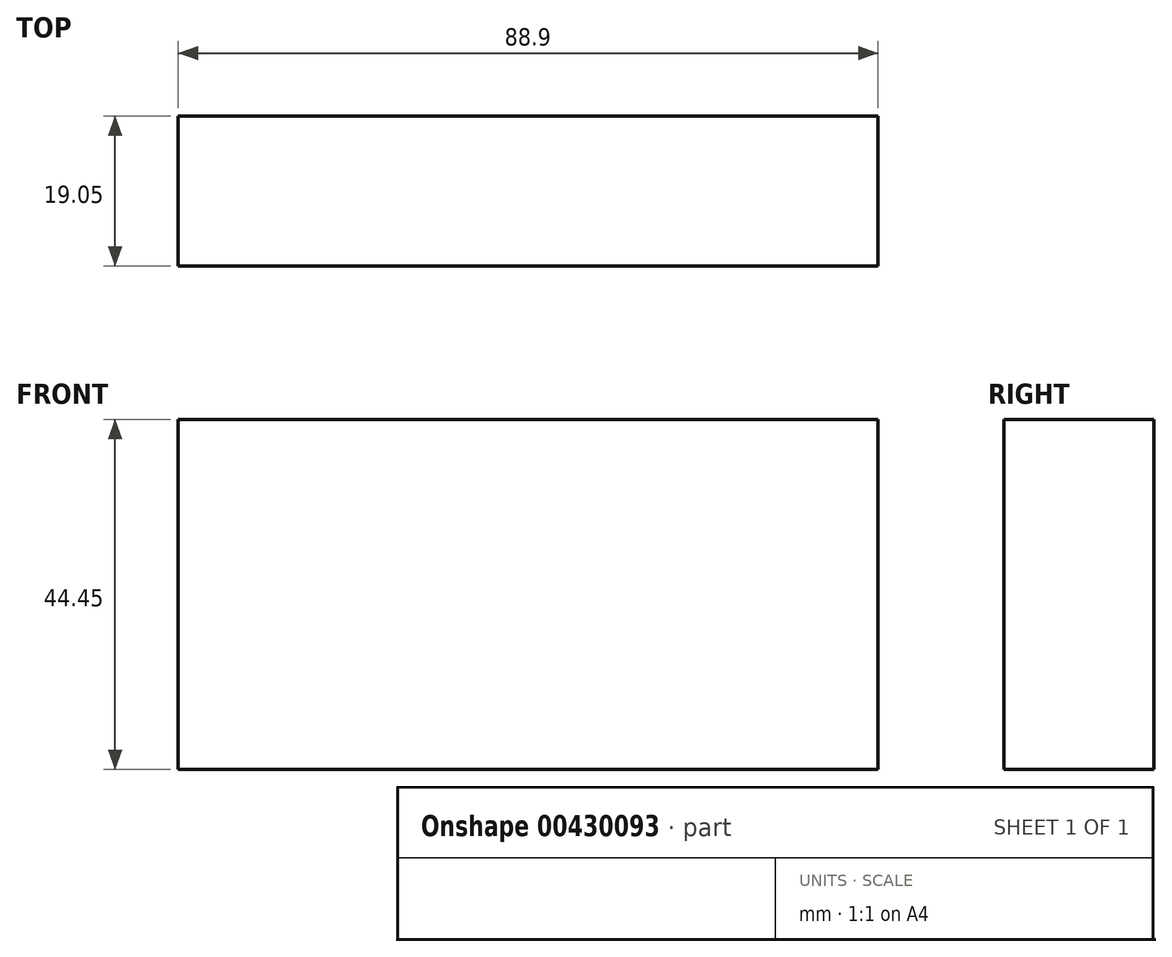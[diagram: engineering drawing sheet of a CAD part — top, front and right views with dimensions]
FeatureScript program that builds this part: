
annotation { "Feature Type Name" : "Feature", "Feature Type Description" : "" }
export const myFeature = defineFeature(function(context is Context, id is Id, definition is map)
    precondition{}
    {
        {
            var Q0;
            Q0=qCreatedBy(makeId("Top.planeOp"),FACE);
            var sketch = newSketch(context, id + "F0", { "sketchPlane" : qUnion([Q0])});
            skLineSegment(sketch, "E0.bottom", {"start": v(0, 0) * mm, "end": v(88.9, 0) * mm});
            skLineSegment(sketch, "E0.top", {"start": v(0, -19.05) * mm, "end": v(88.9, -19.05) * mm});
            skLineSegment(sketch, "E0.left", {"start": v(0, 0) * mm, "end": v(0, -19.05) * mm});
            skLineSegment(sketch, "E0.right", {"start": v(88.9, 0) * mm, "end": v(88.9, -19.05) * mm});
            skSolve(sketch);
        }
        {
            var Q0;
            Q0=makeQuery(id+"F0.imprint","IMPRINT",FACE,{"disambiguationData":[TD([[makeQuery(id+"F0.imprint","IMPRINT",EDGE,{"derivedFrom":sQuery(id+"F0.wireOp",EDGE,"E0.bottom")}),-1.0]])]});
            extrude(context, id + "F1", {"entities" : qUnion([Q0]), "depth" : 44.45 * mm});
        }
    });
